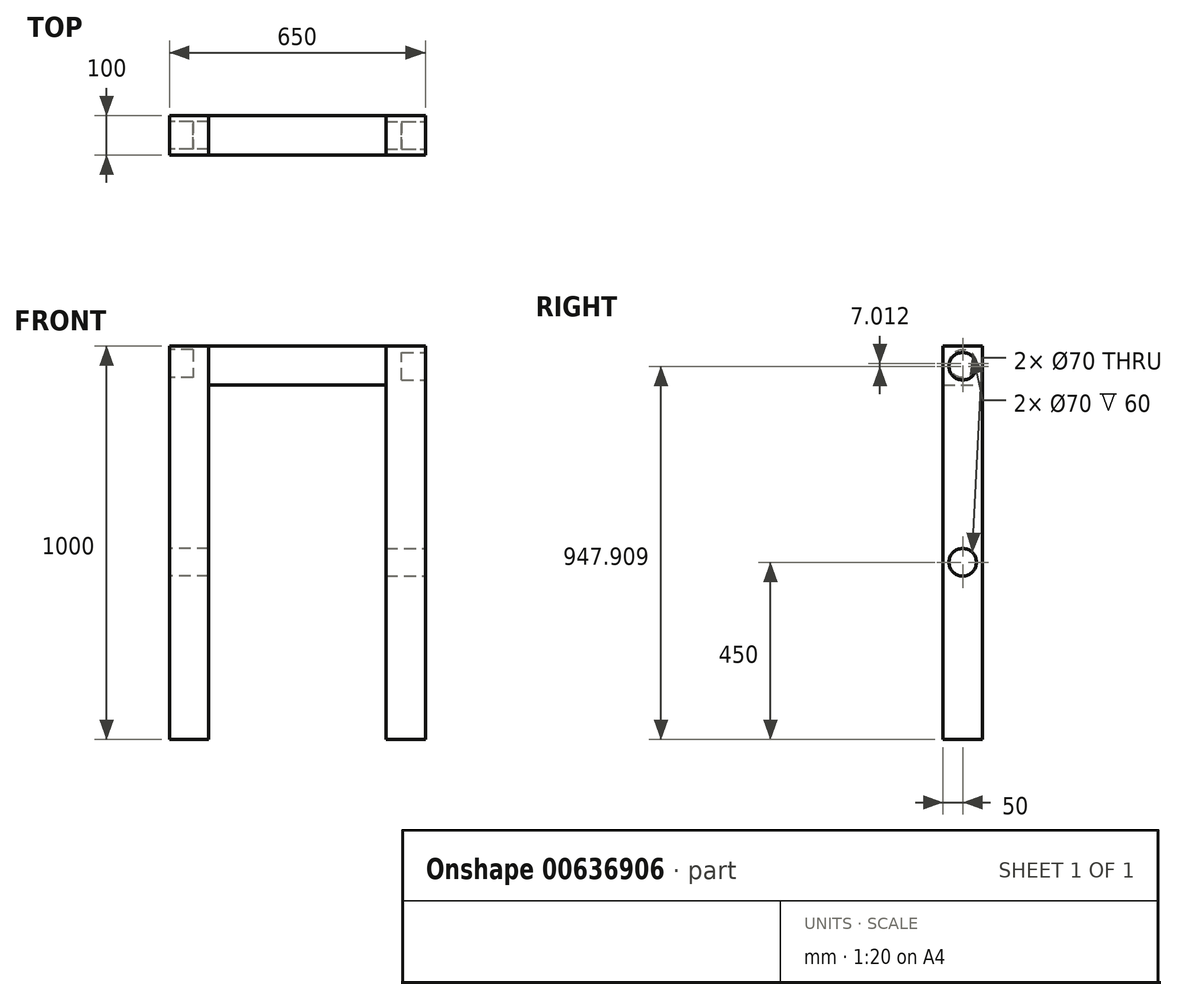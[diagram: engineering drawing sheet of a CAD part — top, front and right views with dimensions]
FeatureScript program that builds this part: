
annotation { "Feature Type Name" : "Feature", "Feature Type Description" : "" }
export const myFeature = defineFeature(function(context is Context, id is Id, definition is map)
    precondition{}
    {
        {
            var Q0;
            Q0=qCreatedBy(makeId("Top.planeOp"),FACE);
            var sketch = newSketch(context, id + "F0", { "sketchPlane" : qUnion([Q0])});
            skLineSegment(sketch, "E0.bottom", {"start": v(-325, 50) * mm, "end": v(-225, 50) * mm});
            skLineSegment(sketch, "E0.top", {"start": v(-325, -50) * mm, "end": v(-225, -50) * mm});
            skLineSegment(sketch, "E0.left", {"start": v(-325, 50) * mm, "end": v(-325, -50) * mm});
            skLineSegment(sketch, "E0.right", {"start": v(-225, 50) * mm, "end": v(-225, -50) * mm});
            skLineSegment(sketch, "E1.bottom", {"start": v(225, 50) * mm, "end": v(325, 50) * mm});
            skLineSegment(sketch, "E1.top", {"start": v(225, -50) * mm, "end": v(325, -50) * mm});
            skLineSegment(sketch, "E1.left", {"start": v(225, 50) * mm, "end": v(225, -50) * mm});
            skLineSegment(sketch, "E1.right", {"start": v(325, 50) * mm, "end": v(325, -50) * mm});
            skSolve(sketch);
        }
        {
            var Q0;
            Q0=makeQuery(id+"F0.imprint","IMPRINT",FACE,{"disambiguationData":[TD([[makeQuery(id+"F0.imprint","IMPRINT",EDGE,{"derivedFrom":sQuery(id+"F0.wireOp",EDGE,"E0.bottom")}),-1.0]])]});
            var Q1;
            Q1=makeQuery(id+"F0.imprint","IMPRINT",FACE,{"disambiguationData":[TD([[makeQuery(id+"F0.imprint","IMPRINT",EDGE,{"derivedFrom":sQuery(id+"F0.wireOp",EDGE,"E1.bottom")}),-1.0]])]});
            extrude(context, id + "F1", {"entities" : qUnion([Q0, Q1]), "depth" : 1000 * mm, "offsetDistance" : 25 * mm});
        }
        {
            var Q0;
            Q0=makeQuery(id+"F1.opExtrude","SWEPT_FACE",FACE,{"disambiguationData":[OSD([sQuery(id+"F0.wireOp",EDGE,"E0.right")])]});
            var sketch = newSketch(context, id + "F2", { "sketchPlane" : qUnion([Q0])});
            skLineSegment(sketch, "E2.bottom", {"start": v(-50, 1000) * mm, "end": v(50, 1000) * mm});
            skLineSegment(sketch, "E2.top", {"start": v(-50, 900) * mm, "end": v(50, 900) * mm});
            skLineSegment(sketch, "E2.left", {"start": v(-50, 1000) * mm, "end": v(-50, 900) * mm});
            skLineSegment(sketch, "E2.right", {"start": v(50, 1000) * mm, "end": v(50, 900) * mm});
            skSolve(sketch);
        }
        {
            var Q0;
            Q0=makeQuery(id+"F2.imprint","IMPRINT",FACE,{"disambiguationData":[TD([[makeQuery(id+"F2.imprint","IMPRINT",EDGE,{"derivedFrom":sQuery(id+"F2.wireOp",EDGE,"E2.bottom")}),1.0]])]});
            extrude(context, id + "F3", {"entities" : qUnion([Q0]), "endBound" : BoundingType.UP_TO_NEXT, "depth" : 25 * mm, "offsetDistance" : 25 * mm});
        }
        {
            var Q0;
            Q0=makeQuery(id+"F1.opExtrude","SWEPT_FACE",FACE,{"disambiguationData":[OSD([sQuery(id+"F0.wireOp",EDGE,"E1.right")])]});
            var sketch = newSketch(context, id + "F4", { "sketchPlane" : qUnion([Q0])});
            skCircle(sketch, "E3", {"center": v(0, 450) * mm, "radius": 35 * mm});
            skSolve(sketch);
        }
        {
            var Q0;
            Q0=makeQuery(id+"F4.imprint","IMPRINT",FACE,{"disambiguationData":[TD([[makeQuery(id+"F4.imprint","IMPRINT",EDGE,{"derivedFrom":sQuery(id+"F4.wireOp",EDGE,"E3")}),1.0]])]});
            extrude(context, id + "F5", {"entities" : qUnion([Q0]), "operationType" : NewBodyOperationType.REMOVE, "endBound" : BoundingType.UP_TO_NEXT, "oppositeDirection" : true, "depth" : 82 * mm, "offsetDistance" : 25 * mm});
        }
        {
            var Q0;
            Q0=makeQuery(id+"F1.opExtrude","SWEPT_FACE",FACE,{"disambiguationData":[OSD([sQuery(id+"F0.wireOp",EDGE,"E0.left")])]});
            var sketch = newSketch(context, id + "F6", { "sketchPlane" : qUnion([Q0])});
            skCircle(sketch, "E4", {"center": v(0, 450) * mm, "radius": 35 * mm});
            skSolve(sketch);
        }
        {
            var Q0;
            Q0=makeQuery(id+"F6.imprint","IMPRINT",FACE,{"disambiguationData":[TD([[makeQuery(id+"F6.imprint","IMPRINT",EDGE,{"derivedFrom":sQuery(id+"F6.wireOp",EDGE,"E4")}),1.0]])]});
            extrude(context, id + "F7", {"entities" : qUnion([Q0]), "operationType" : NewBodyOperationType.REMOVE, "endBound" : BoundingType.UP_TO_NEXT, "oppositeDirection" : true, "depth" : 25 * mm, "offsetDistance" : 25 * mm});
        }
        {
            var Q0;
            Q0=makeQuery(id+"F1.opExtrude","SWEPT_FACE",FACE,{"disambiguationData":[OSD([sQuery(id+"F0.wireOp",EDGE,"E0.left")])]});
            var sketch = newSketch(context, id + "F8", { "sketchPlane" : qUnion([Q0])});
            skCircle(sketch, "E5", {"center": v(0, 954.92) * mm, "radius": 35 * mm});
            skSolve(sketch);
        }
        {
            var Q0;
            Q0=makeQuery(id+"F8.imprint","IMPRINT",FACE,{"disambiguationData":[TD([[makeQuery(id+"F8.imprint","IMPRINT",EDGE,{"derivedFrom":sQuery(id+"F8.wireOp",EDGE,"E5")}),1.0]])]});
            extrude(context, id + "F9", {"entities" : qUnion([Q0]), "operationType" : NewBodyOperationType.REMOVE, "oppositeDirection" : true, "depth" : 60 * mm, "offsetDistance" : 25 * mm});
        }
        {
            var Q0;
            Q0=makeQuery(id+"F1.opExtrude","SWEPT_FACE",FACE,{"disambiguationData":[OSD([sQuery(id+"F0.wireOp",EDGE,"E1.right")])]});
            var sketch = newSketch(context, id + "F10", { "sketchPlane" : qUnion([Q0])});
            skCircle(sketch, "E6", {"center": v(0, 947.9) * mm, "radius": 35 * mm});
            skSolve(sketch);
        }
        {
            var Q0;
            Q0=makeQuery(id+"F10.imprint","IMPRINT",FACE,{"disambiguationData":[TD([[makeQuery(id+"F10.imprint","IMPRINT",EDGE,{"derivedFrom":sQuery(id+"F10.wireOp",EDGE,"E6")}),1.0]])]});
            extrude(context, id + "F11", {"entities" : qUnion([Q0]), "operationType" : NewBodyOperationType.REMOVE, "oppositeDirection" : true, "depth" : 60 * mm, "offsetDistance" : 25 * mm});
        }
    });
